# Revit family: POR_Matura_P0982_BIM_FR
name_source: partatom
category: Plumbing Fixtures
revit_build: Autodesk Revit 2017 (Build: 20160225_1515(x64)
units: mm (PartAtom-declared; Revit-internal decimal feet)

## family parameters
Always vertical = No
Cut with Voids When Loaded = No
OmniClass Number = 23.45.05.21.11.11
OmniClass Title = Water Operated Water Closets
Part Type = Normal
Room Calculation Point = No
Round Connector Dimension = Use Diameter
Shared = No
Work Plane-Based = No

## types (1)
- P098201 - MATURA, Cuvette seule
    Accessoires = http://www.porcher.com
    Auteur = Ideal Standard
    BIMobject category = Toilets
    BIMobject category code = sanitary-toilets
    BIMobject main category = Sanitary
    BIMobject main category code = sanitary
    BOSUseNativeGeometries = 1
    Bim-NomDuProjet = POR_Porcher_WCs_P098201
    Brand url = http://www.porcher.com
    Caractéristiques = Cuvette seule
    CodeBarre = 3391500577800
    Conformité = NF
    ConseilsDInstallation = www.idealspec.fr
    Cost = 0 $
    Couleur = Blanc
    CoûtDeRemplacement = 0
    Date of publishing = 2018_05_23
    DateDeCréation = 2018_05_23
    Description = MATURA - Cuvette seule
    Dimensions = 384 x 355 x 700mm
    DuréeGarantie = ans
    DétailGarantie = Constructeur
    EAN code = https://3391500577800
    Edition number = 1
    Espace = Interne
    Forme = Complexe
    Hauteur = 384 mm
    IFC Classification = Sanitary Terminal
    IfcExportAs = IfcSanitaryTerminalType
    IfcExportType = Toilets
    InformationsProduit = www.idealspec.fr
    Installation instructions = http://www.idealspec.fr
    Largeur = 355 mm  [stored 1.1647 ft]
    Longueur = 700 mm  [stored 2.29659 ft]
    Manufacturer name = Porcher
    Marque = PORCHER
    Masterformat 2014 Code = 10 28 13
    Masterformat 2014 Description = Toilet Accessories
    Material main = Ceramics
    Matériel = Ceramics
    Model = P098201
    NBS Reference Code = 35-93-94
    NBS Reference Description = Wc Pans
    Nom = POR_Porcher_WCs_P098201
    Nominal height = 355
    Nominal width = 700
    OmniClass Code = 23-31 19 00
    OmniClass Description = Toilets
    PerformanceAccessibilité = NF
    PoidsNet = 23.5 Kg
    Product Guid = b9aec397-e124-4a89-bb43-c2be7b5a65ed
    Product SKU = P0982
    Product certification = http://www.idealspec.fr
    Product data url = https://bimobject.com
    Product family = MATURA
    Product group = Toilets
    Product name = MATURA - Cuvette seule
    Product url = http://www.idealspec.fr
    Profondeur = 0 mm  [stored 0 ft]
    QR code = http://bimobject.com
    Raccordement = Plomberie
    Référence = P098201
    Révision = 1
    Technical description = http://www.idealspec.fr
    TypeDImmobilisation = Fixe
    URL = http://www.porcher.com
    Uniclass 1.4 Code = L7216
    Uniclass 1.4 Description = Toilets
    Uniclass 2.0 Code = PR-35-93-94
    Uniclass 2.0 Description = Wc Pans
    Uniclass 2015 Code = Pr_40_20_93_94
    Uniclass 2015 Name = WC pans
    Uniclass2015Code = Pr_40_20_93_94
    Uniclass2015Title = WC pans
    Uniclass2015Version = Products v1.1
    UnitéDeTemps = an
    UrlDuFabricant = http://www.porcher.com
    Version = 1
    Weight Net (Kg) = 23.5

note: [stored X ft] marks values corroborated as IEEE doubles in the binary element streams (Revit-internal decimal feet)

## geometry (parser evidence)
native form markers: Sweep x4
no freeform markers — native parametric forms only
